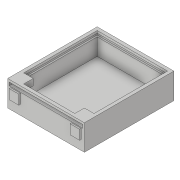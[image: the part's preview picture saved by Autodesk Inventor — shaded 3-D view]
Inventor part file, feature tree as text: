
AUTODESK INVENTOR PART (.ipt)
format: ipt  version: 2018.3 (Build 223284000, 284)  size: 150,528 bytes
history: native  units: in
note: dims shown in document units (in); Inventor stores cm internally (conversion verified against a paired STEP export)
features: extrude x5, sketch x5
ambient origin geometry x8: Origin, YZ Plane, XZ Plane, XY Plane, X Axis, Y Axis, Z Axis, Center Point
bodies: Solid1 (feature_tree)
feature tree (10):
  extrude  "Extrusion1"  Depth=1.0in
  extrude  "Extrusion2"  Depth=0.125in
  extrude  "Extrusion3"  Depth=0.125in
  extrude  "Extrusion4"  Depth=0.875in TaperAngle=0.0deg
  extrude  "Extrusion5"  Depth=0.0625in
  sketch  "Sketch1"  dims[d0=3.0in d1=1.0in]
  sketch  "Sketch2"  dims[d2=3.5in d3=0.0in d4=0.125in]
  sketch  "Sketch3"  dims[d5=0.125in d6=0.125in]
  sketch  "Sketch5"  dims[d7=0.125in d8=0.875in d9=0.0in]
  sketch  "Sketch6"  dims[d46=0.125in d47=0.0625in d49=0.0625in d50=3.4375in d51=0.0in d62=0.25in d64=0.375in d65=0.25in d66=0.0in d67=0.375in d68=0.375in d69=0.375in d70=0.375in d71=0.375in d72=0.375in d73=0.375in d74=0.0625in d75=0.0in]
